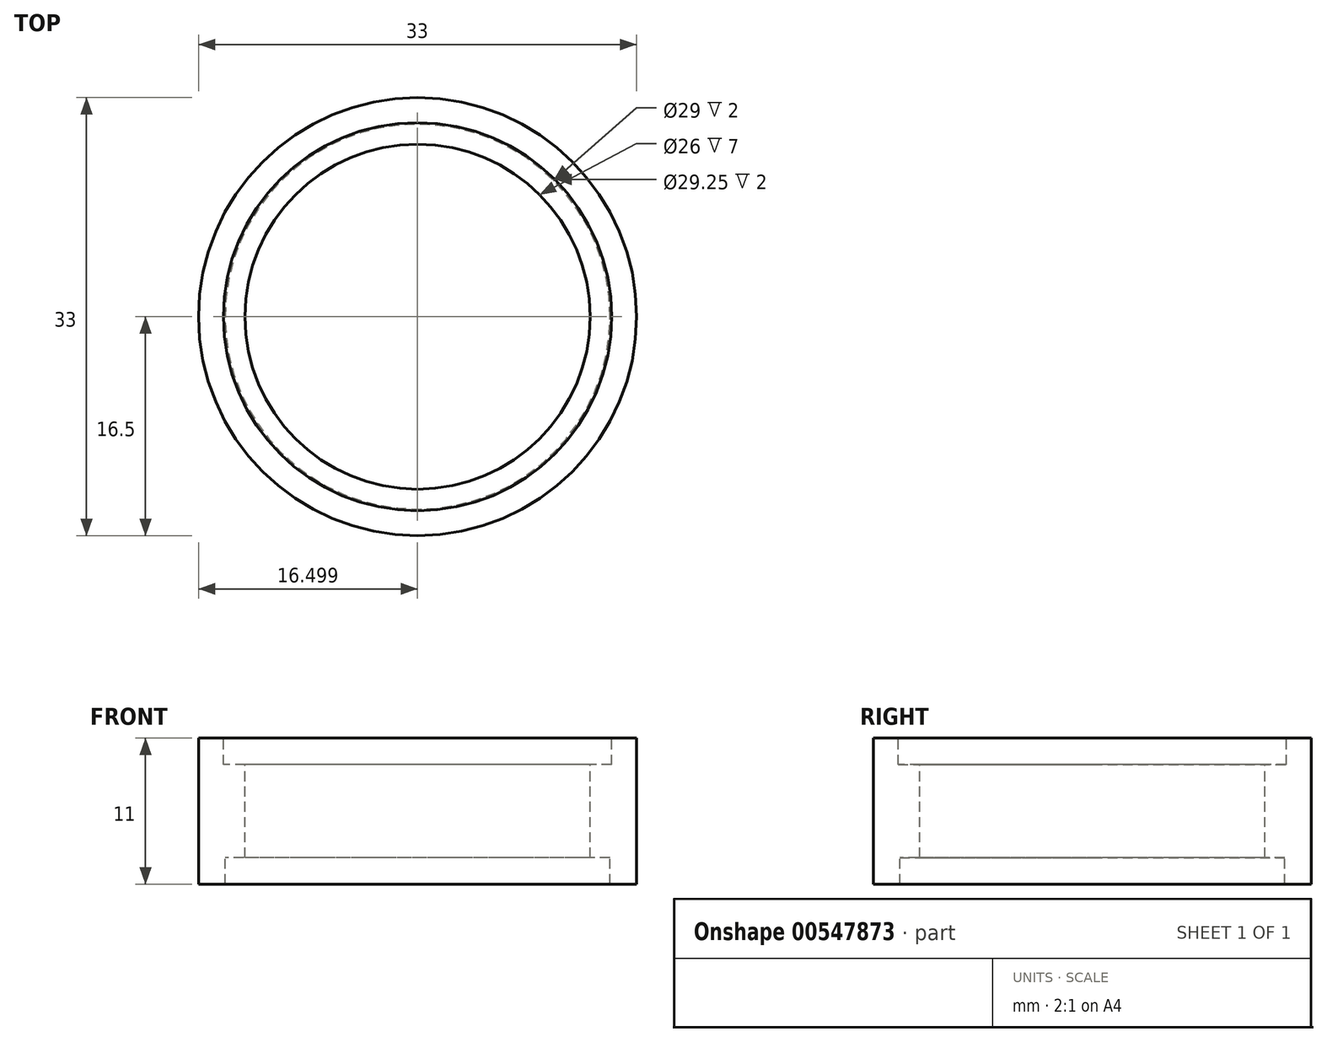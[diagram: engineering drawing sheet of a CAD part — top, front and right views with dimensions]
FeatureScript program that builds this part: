
annotation { "Feature Type Name" : "Feature", "Feature Type Description" : "" }
export const myFeature = defineFeature(function(context is Context, id is Id, definition is map)
    precondition{}
    {
        {
            var Q0;
            Q0=qCreatedBy(makeId("Front.planeOp"),FACE);
            var sketch = newSketch(context, id + "F0", { "sketchPlane" : qUnion([Q0])});
            skLineSegment(sketch, "E0", {"start": v(-23.76, -4.16) * mm, "end": v(-23.76, -2.16) * mm});
            skLineSegment(sketch, "E1", {"start": v(-23.76, -2.16) * mm, "end": v(-22.26, -2.16) * mm});
            skLineSegment(sketch, "E2", {"start": v(-22.26, -2.16) * mm, "end": v(-22.26, 4.84) * mm});
            skLineSegment(sketch, "E3", {"start": v(-22.26, 4.84) * mm, "end": v(-23.89, 4.84) * mm});
            skLineSegment(sketch, "E4", {"start": v(-23.89, 4.84) * mm, "end": v(-23.89, 6.84) * mm});
            skLineSegment(sketch, "E5", {"start": v(-23.89, 6.84) * mm, "end": v(-25.76, 6.84) * mm});
            skLineSegment(sketch, "E6", {"start": v(-25.76, 6.84) * mm, "end": v(-25.76, -4.16) * mm});
            skLineSegment(sketch, "E7", {"start": v(-25.76, -4.16) * mm, "end": v(-23.76, -4.16) * mm});
            skLineSegment(sketch, "E8", {"start": v(-9.26, 9.95) * mm, "end": v(-9.26, -7.28) * mm, "construction": true});
            skSolve(sketch);
        }
        {
            var Q0;
            Q0=makeQuery(id+"F0.imprint","IMPRINT",FACE,{"disambiguationData":[TD([[makeQuery(id+"F0.imprint","IMPRINT",EDGE,{"derivedFrom":sQuery(id+"F0.wireOp",EDGE,"E0")}),1.0]])]});
            var Q1;
            Q1=sQuery(id+"F0.wireOp",EDGE,"E8");
            revolve(context, id + "F1", {"surfaceOperationType" : NewSurfaceOperationType.NEW, "entities" : qUnion([Q0]), "axis" : qUnion([Q1]), "revolveType" : RevolveType.FULL});
        }
    });
